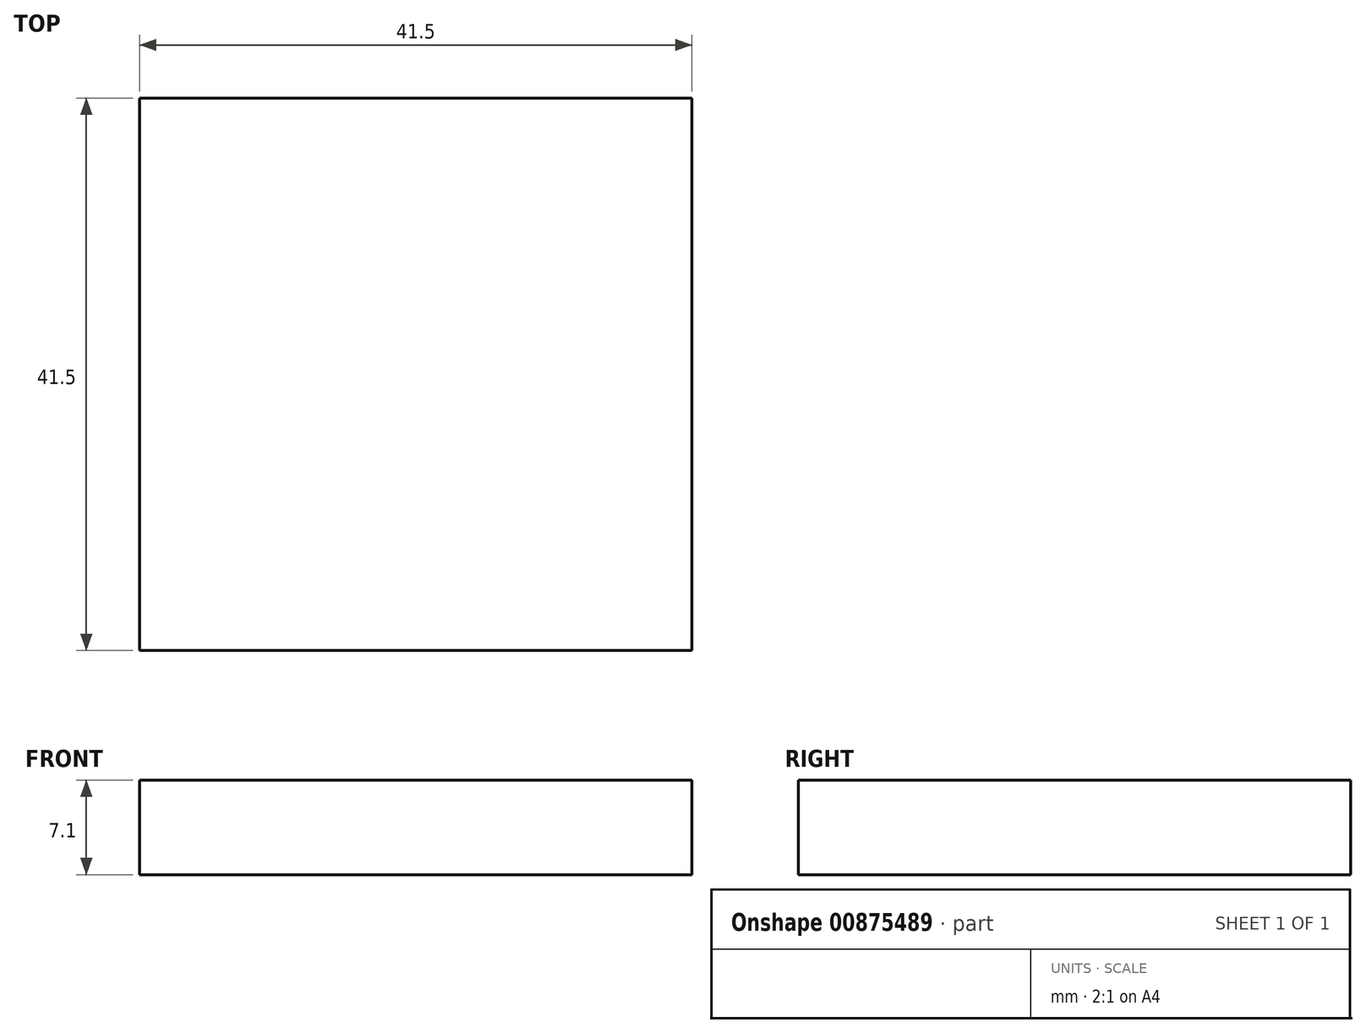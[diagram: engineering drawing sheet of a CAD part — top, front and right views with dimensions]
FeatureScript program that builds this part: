
annotation { "Feature Type Name" : "Feature", "Feature Type Description" : "" }
export const myFeature = defineFeature(function(context is Context, id is Id, definition is map)
    precondition{}
    {
        {
            var Q0;
            Q0=qCreatedBy(makeId("Top.planeOp"),FACE);
            var sketch = newSketch(context, id + "F0", { "sketchPlane" : qUnion([Q0])});
            skLineSegment(sketch, "E0.bottom", {"start": v(20.75, 20.75) * mm, "end": v(-20.75, 20.75) * mm});
            skLineSegment(sketch, "E0.top", {"start": v(20.75, -20.75) * mm, "end": v(-20.75, -20.75) * mm});
            skLineSegment(sketch, "E0.left", {"start": v(20.75, 20.75) * mm, "end": v(20.75, -20.75) * mm});
            skLineSegment(sketch, "E0.right", {"start": v(-20.75, 20.75) * mm, "end": v(-20.75, -20.75) * mm});
            skPoint(sketch, "E0.middle", {"position": v(0, 0) * mm});
            skSolve(sketch);
        }
        {
            var Q0;
            Q0=makeQuery(id+"F0.imprint","IMPRINT",FACE,{"disambiguationData":[TD([[makeQuery(id+"F0.imprint","IMPRINT",EDGE,{"derivedFrom":sQuery(id+"F0.wireOp",EDGE,"E0.bottom")}),1.0]])]});
            extrude(context, id + "F1", {"entities" : qUnion([Q0]), "depth" : 7.1 * mm, "offsetDistance" : 25 * mm});
        }
    });
